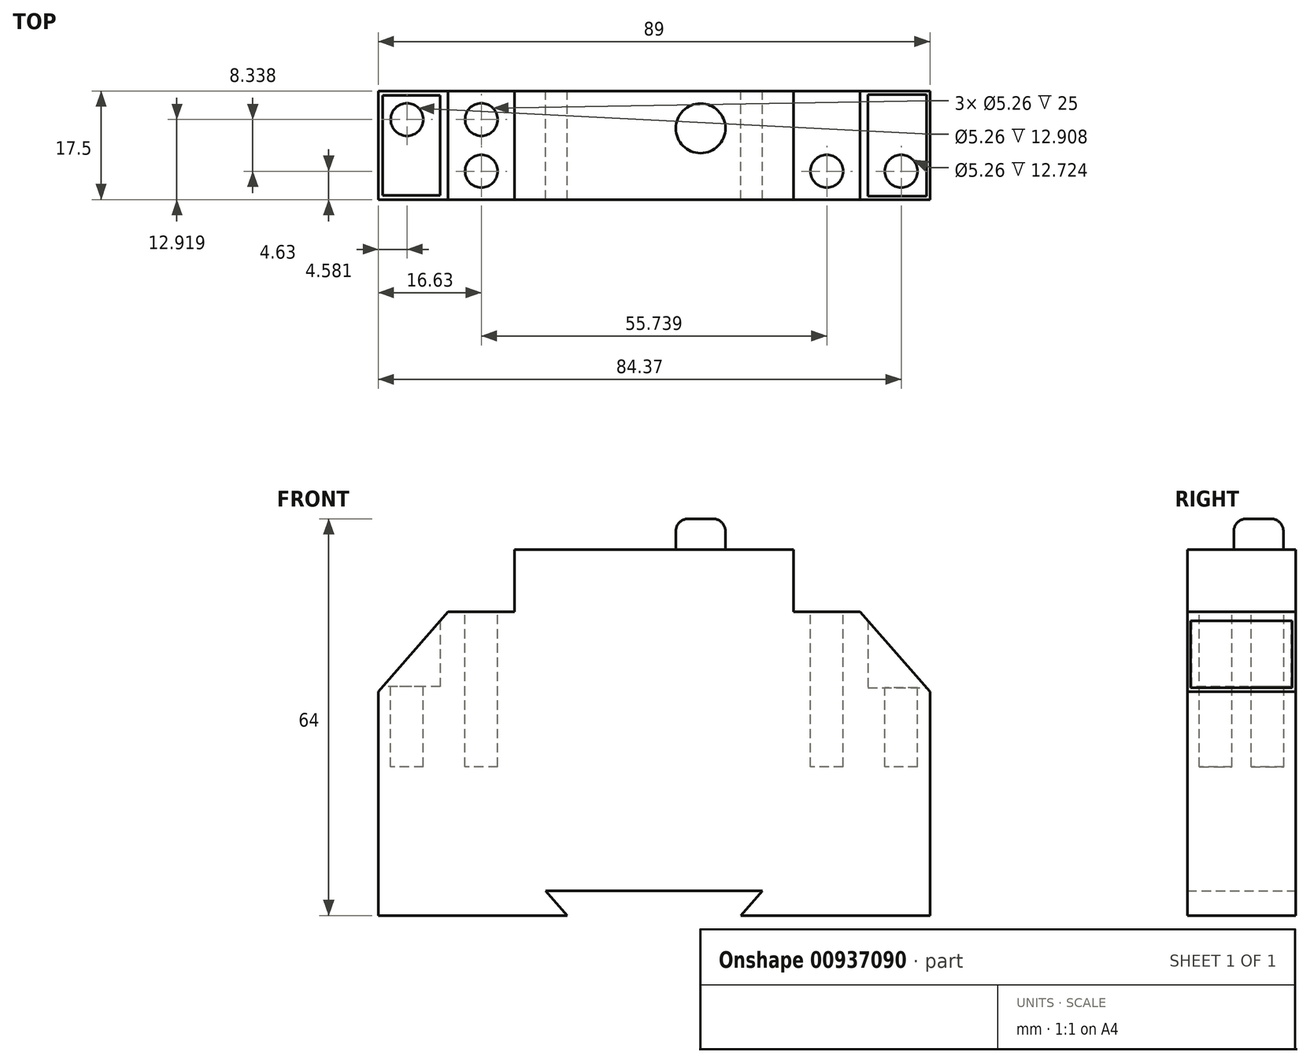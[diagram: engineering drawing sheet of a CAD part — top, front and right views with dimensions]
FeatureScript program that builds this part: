
annotation { "Feature Type Name" : "Feature", "Feature Type Description" : "" }
export const myFeature = defineFeature(function(context is Context, id is Id, definition is map)
    precondition{}
    {
        {
            var Q0;
            Q0=qCreatedBy(makeId("Front.planeOp"),FACE);
            var sketch = newSketch(context, id + "F0", { "sketchPlane" : qUnion([Q0])});
            skLineSegment(sketch, "E0.bottom", {"start": v(22.5, 29.5) * mm, "end": v(-22.5, 29.5) * mm});
            skLineSegment(sketch, "E0.top", {"start": v(44.5, -29.5) * mm, "end": v(14, -29.5) * mm});
            skLineSegment(sketch, "E0.left", {"start": v(44.5, 6.61) * mm, "end": v(44.5, -29.5) * mm});
            skLineSegment(sketch, "E0.right", {"start": v(-44.5, 6.61) * mm, "end": v(-44.5, -29.5) * mm});
            skPoint(sketch, "E0.middle", {"position": v(0, 0) * mm});
            skLineSegment(sketch, "E1.left", {"start": v(22.5, 19.5) * mm, "end": v(22.5, 29.5) * mm});
            skLineSegment(sketch, "E1.right", {"start": v(-22.5, 19.5) * mm, "end": v(-22.5, 29.5) * mm});
            skPoint(sketch, "E1.middle", {"position": v(0, 29.5) * mm});
            skLineSegment(sketch, "E2", {"start": v(-22.5, 19.5) * mm, "end": v(-33.24, 19.5) * mm});
            skLineSegment(sketch, "E3", {"start": v(-33.24, 19.5) * mm, "end": v(-44.5, 6.61) * mm});
            skLineSegment(sketch, "E4.MirrorCS", {"start": v(22.5, 19.5) * mm, "end": v(33.24, 19.5) * mm});
            skLineSegment(sketch, "E5.MirrorCS", {"start": v(33.24, 19.5) * mm, "end": v(44.5, 6.61) * mm});
            skPoint(sketch, "E6.orphan", {"position": v(-44.5, 29.5) * mm});
            skPoint(sketch, "E7.orphan", {"position": v(44.5, 29.5) * mm});
            skPoint(sketch, "E8.orphan", {"position": v(22.5, 39.5) * mm});
            skPoint(sketch, "E9.orphan", {"position": v(-22.5, 39.5) * mm});
            skPoint(sketch, "E10.middle", {"position": v(0, -29.5) * mm});
            skLineSegment(sketch, "E11", {"start": v(-17.5, -25.5) * mm, "end": v(-14, -29.5) * mm});
            skLineSegment(sketch, "E12.MirrorCS", {"start": v(17.5, -25.5) * mm, "end": v(14, -29.5) * mm});
            skLineSegment(sketch, "E13", {"start": v(-17.5, -25.5) * mm, "end": v(17.5, -25.5) * mm});
            skLineSegment(sketch, "E14.trimOffspring", {"start": v(-14, -29.5) * mm, "end": v(-44.5, -29.5) * mm});
            skSolve(sketch);
        }
        {
            var Q0;
            Q0=makeQuery(id+"F0.imprint","IMPRINT",FACE,{"disambiguationData":[TD([[makeQuery(id+"F0.imprint","IMPRINT",EDGE,{"derivedFrom":sQuery(id+"F0.wireOp",EDGE,"E0.bottom")}),1.0]])]});
            extrude(context, id + "F1", {"entities" : qUnion([Q0]), "endBound" : BoundingType.SYMMETRIC, "depth" : 17.5 * mm, "offsetDistance" : 25 * mm});
        }
        {
            var Q0;
            Q0=makeQuery(id+"F1.opExtrude","SWEPT_FACE",FACE,{"disambiguationData":[OSD([sQuery(id+"F0.wireOp",EDGE,"E0.left")])]});
            var sketch = newSketch(context, id + "F2", { "sketchPlane" : qUnion([Q0])});
            skLineSegment(sketch, "E15.bottom", {"start": v(8.75, 6.61) * mm, "end": v(-8.75, 6.61) * mm});
            skLineSegment(sketch, "E15.top", {"start": v(8.75, 19.51) * mm, "end": v(-8.75, 19.51) * mm});
            skLineSegment(sketch, "E15.left", {"start": v(8.75, 6.61) * mm, "end": v(8.75, 19.51) * mm});
            skLineSegment(sketch, "E15.right", {"start": v(-8.75, 6.61) * mm, "end": v(-8.75, 19.51) * mm});
            skPoint(sketch, "E16.middle", {"position": v(0, 16.61) * mm});
            skLineSegment(sketch, "E17", {"start": v(-8.75, 13.06) * mm, "end": v(8.75, 13.06) * mm});
            skLineSegment(sketch, "E18.bottom", {"start": v(8.2, 18.9) * mm, "end": v(-8.2, 18.9) * mm});
            skLineSegment(sketch, "E18.top", {"start": v(8.2, 7.22) * mm, "end": v(-8.2, 7.22) * mm});
            skLineSegment(sketch, "E18.left", {"start": v(8.2, 18.9) * mm, "end": v(8.2, 7.22) * mm});
            skLineSegment(sketch, "E18.right", {"start": v(-8.2, 18.9) * mm, "end": v(-8.2, 7.22) * mm});
            skPoint(sketch, "E18.middle", {"position": v(0, 13.06) * mm});
            skSolve(sketch);
        }
        {
            var Q0;
            {var subQ5=sQuery(id+"F2.wireOp",EDGE,"E16.bottom");Q0=makeQuery(id+"F2.imprint","IMPRINT",FACE,{"disambiguationData":[TD([[makeQuery(id+"F2.imprint","IMPRINT",EDGE,{"derivedFrom":subQ5}),1.0]])]});}
            var Q1;
            {var subQ5=sQuery(id+"F2.wireOp",EDGE,"E16.top");Q1=makeQuery(id+"F2.imprint","IMPRINT",FACE,{"disambiguationData":[TD([[makeQuery(id+"F2.imprint","IMPRINT",EDGE,{"derivedFrom":subQ5}),-1.0]])]});}
            var Q2;
            {var subQ5=sQuery(id+"F2.wireOp",EDGE,"E18.bottom");Q2=makeQuery(id+"F2.imprint","IMPRINT",FACE,{"disambiguationData":[TD([[makeQuery(id+"F2.imprint","IMPRINT",EDGE,{"derivedFrom":subQ5}),1.0]])]});}
            var Q3;
            {var subQ5=sQuery(id+"F2.wireOp",EDGE,"E18.top");Q3=makeQuery(id+"F2.imprint","IMPRINT",FACE,{"disambiguationData":[TD([[makeQuery(id+"F2.imprint","IMPRINT",EDGE,{"derivedFrom":subQ5}),-1.0]])]});}
            extrude(context, id + "F3", {"entities" : qUnion([Q0, Q1, Q2, Q3]), "operationType" : NewBodyOperationType.REMOVE, "oppositeDirection" : true, "depth" : 10 * mm, "offsetDistance" : 25 * mm});
        }
        {
            var Q0;
            Q0=makeQuery(id+"F1.opExtrude","SWEPT_FACE",FACE,{"disambiguationData":[OSD([sQuery(id+"F0.wireOp",EDGE,"E0.right")])]});
            var sketch = newSketch(context, id + "F4", { "sketchPlane" : qUnion([Q0])});
            skLineSegment(sketch, "E19.bottom", {"start": v(8.75, 6.61) * mm, "end": v(-8.75, 6.61) * mm});
            skLineSegment(sketch, "E19.top", {"start": v(8.75, 19.51) * mm, "end": v(-8.75, 19.51) * mm});
            skLineSegment(sketch, "E19.left", {"start": v(8.75, 6.61) * mm, "end": v(8.75, 19.51) * mm});
            skLineSegment(sketch, "E19.right", {"start": v(-8.75, 6.61) * mm, "end": v(-8.75, 19.51) * mm});
            skPoint(sketch, "E20.middle", {"position": v(0, 13.06) * mm});
            skLineSegment(sketch, "E21", {"start": v(-8.75, 13.06) * mm, "end": v(8.75, 13.06) * mm});
            skLineSegment(sketch, "E22.bottom", {"start": v(8.04, 18.72) * mm, "end": v(-8.04, 18.72) * mm});
            skLineSegment(sketch, "E22.top", {"start": v(8.04, 7.4) * mm, "end": v(-8.04, 7.4) * mm});
            skLineSegment(sketch, "E22.left", {"start": v(8.04, 18.72) * mm, "end": v(8.04, 7.4) * mm});
            skLineSegment(sketch, "E22.right", {"start": v(-8.04, 18.72) * mm, "end": v(-8.04, 7.4) * mm});
            skSolve(sketch);
        }
        {
            var Q0;
            {var subQ5=sQuery(id+"F4.wireOp",EDGE,"E20.bottom");Q0=makeQuery(id+"F4.imprint","IMPRINT",FACE,{"disambiguationData":[TD([[makeQuery(id+"F4.imprint","IMPRINT",EDGE,{"derivedFrom":subQ5}),1.0]])]});}
            var Q1;
            {var subQ5=sQuery(id+"F4.wireOp",EDGE,"E20.top");Q1=makeQuery(id+"F4.imprint","IMPRINT",FACE,{"disambiguationData":[TD([[makeQuery(id+"F4.imprint","IMPRINT",EDGE,{"derivedFrom":subQ5}),-1.0]])]});}
            var Q2;
            {var subQ5=sQuery(id+"F4.wireOp",EDGE,"E22.bottom");Q2=makeQuery(id+"F4.imprint","IMPRINT",FACE,{"disambiguationData":[TD([[makeQuery(id+"F4.imprint","IMPRINT",EDGE,{"derivedFrom":subQ5}),1.0]])]});}
            var Q3;
            {var subQ5=sQuery(id+"F4.wireOp",EDGE,"E22.top");Q3=makeQuery(id+"F4.imprint","IMPRINT",FACE,{"disambiguationData":[TD([[makeQuery(id+"F4.imprint","IMPRINT",EDGE,{"derivedFrom":subQ5}),-1.0]])]});}
            extrude(context, id + "F5", {"entities" : qUnion([Q0, Q1, Q2, Q3]), "operationType" : NewBodyOperationType.REMOVE, "oppositeDirection" : true, "depth" : 10 * mm, "offsetDistance" : 25 * mm});
        }
        {
            var Q0;
            Q0=makeQuery(id+"F1.opExtrude","SWEPT_FACE",FACE,{"disambiguationData":[OSD([sQuery(id+"F0.wireOp",EDGE,"E2")])]});
            var sketch = newSketch(context, id + "F6", { "sketchPlane" : qUnion([Q0])});
            skLineSegment(sketch, "E23", {"start": v(-27.87, 8.75) * mm, "end": v(-27.87, -8.75) * mm});
            skCircle(sketch, "E24", {"center": v(-27.87, 4.17) * mm, "radius": 2.63 * mm});
            skCircle(sketch, "E25.MirrorC", {"center": v(-27.87, -4.17) * mm, "radius": 2.63 * mm});
            skCircle(sketch, "E26.1.0.0", {"center": v(-39.87, 4.17) * mm, "radius": 2.63 * mm});
            skCircle(sketch, "E26.1.0.1", {"center": v(-39.87, -4.17) * mm, "radius": 2.63 * mm});
            skLineSegment(sketch, "E26.direction1", {"start": v(-27.87, -4.17) * mm, "end": v(-39.87, -4.17) * mm, "construction": true});
            skCircle(sketch, "E27.MirrorC", {"center": v(27.87, 4.17) * mm, "radius": 2.63 * mm});
            skCircle(sketch, "E28.MirrorC", {"center": v(27.87, -4.17) * mm, "radius": 2.63 * mm});
            skCircle(sketch, "E29.MirrorC", {"center": v(39.87, 4.17) * mm, "radius": 2.63 * mm});
            skCircle(sketch, "E30.MirrorC", {"center": v(39.87, -4.17) * mm, "radius": 2.63 * mm});
            skSolve(sketch);
        }
        {
            var Q0;
            {var subQ0=sQuery(id+"F6.wireOp",EDGE,"E25.MirrorC");var subQ1=sQuery(id+"F6.wireOp",EDGE,"E23");var subQ2=makeQuery(id+"F6.imprint","INTERSECT",VERTEX,{"disambiguationData":[OD(0.0)],"derivedFrom":[subQ1,subQ0]});Q0=makeQuery(id+"F6.imprint","IMPRINT",FACE,{"disambiguationData":[TD([[makeQuery(id+"F6.imprint","IMPRINT",EDGE,{"disambiguationData":[TD([[subQ2,-1.0]])],"derivedFrom":subQ1}),1.0]])]});}
            var Q1;
            {var subQ0=sQuery(id+"F6.wireOp",EDGE,"E25.MirrorC");var subQ1=sQuery(id+"F6.wireOp",EDGE,"E23");var subQ2=makeQuery(id+"F6.imprint","INTERSECT",VERTEX,{"disambiguationData":[OD(0.0)],"derivedFrom":[subQ1,subQ0]});Q1=makeQuery(id+"F6.imprint","IMPRINT",FACE,{"disambiguationData":[TD([[makeQuery(id+"F6.imprint","IMPRINT",EDGE,{"disambiguationData":[TD([[subQ2,-1.0]])],"derivedFrom":subQ1}),-1.0]])]});}
            var Q2;
            {var subQ0=sQuery(id+"F6.wireOp",EDGE,"E24");var subQ1=sQuery(id+"F6.wireOp",EDGE,"E23");var subQ2=makeQuery(id+"F6.imprint","INTERSECT",VERTEX,{"disambiguationData":[OD(0.0)],"derivedFrom":[subQ1,subQ0]});Q2=makeQuery(id+"F6.imprint","IMPRINT",FACE,{"disambiguationData":[TD([[makeQuery(id+"F6.imprint","IMPRINT",EDGE,{"disambiguationData":[TD([[subQ2,-1.0]])],"derivedFrom":subQ1}),-1.0]])]});}
            var Q3;
            {var subQ0=sQuery(id+"F6.wireOp",EDGE,"E24");var subQ1=sQuery(id+"F6.wireOp",EDGE,"E23");var subQ2=makeQuery(id+"F6.imprint","INTERSECT",VERTEX,{"disambiguationData":[OD(0.0)],"derivedFrom":[subQ1,subQ0]});Q3=makeQuery(id+"F6.imprint","IMPRINT",FACE,{"disambiguationData":[TD([[makeQuery(id+"F6.imprint","IMPRINT",EDGE,{"disambiguationData":[TD([[subQ2,-1.0]])],"derivedFrom":subQ1}),1.0]])]});}
            var Q4;
            Q4=makeQuery(id+"F6.imprint","IMPRINT",FACE,{"disambiguationData":[TD([[makeQuery(id+"F6.imprint","IMPRINT",EDGE,{"derivedFrom":sQuery(id+"F6.wireOp",EDGE,"E26.1.0.0")}),1.0]])]});
            var Q5;
            Q5=makeQuery(id+"F6.imprint","IMPRINT",FACE,{"disambiguationData":[TD([[makeQuery(id+"F6.imprint","IMPRINT",EDGE,{"derivedFrom":sQuery(id+"F6.wireOp",EDGE,"E26.1.0.1")}),-1.0]])]});
            var Q6;
            Q6=makeQuery(id+"F6.imprint","IMPRINT",FACE,{"disambiguationData":[TD([[makeQuery(id+"F6.imprint","IMPRINT",EDGE,{"derivedFrom":sQuery(id+"F6.wireOp",EDGE,"E27.MirrorC")}),-1.0]])]});
            var Q7;
            Q7=makeQuery(id+"F6.imprint","IMPRINT",FACE,{"disambiguationData":[TD([[makeQuery(id+"F6.imprint","IMPRINT",EDGE,{"derivedFrom":sQuery(id+"F6.wireOp",EDGE,"E28.MirrorC")}),1.0]])]});
            var Q8;
            Q8=makeQuery(id+"F6.imprint","IMPRINT",FACE,{"disambiguationData":[TD([[makeQuery(id+"F6.imprint","IMPRINT",EDGE,{"derivedFrom":sQuery(id+"F6.wireOp",EDGE,"E29.MirrorC")}),-1.0]])]});
            var Q9;
            Q9=makeQuery(id+"F6.imprint","IMPRINT",FACE,{"disambiguationData":[TD([[makeQuery(id+"F6.imprint","IMPRINT",EDGE,{"derivedFrom":sQuery(id+"F6.wireOp",EDGE,"E30.MirrorC")}),1.0]])]});
            extrude(context, id + "F7", {"entities" : qUnion([Q0, Q1, Q2, Q3, Q4, Q5, Q6, Q7, Q8, Q9]), "operationType" : NewBodyOperationType.REMOVE, "oppositeDirection" : true, "depth" : 25 * mm, "offsetDistance" : 25 * mm});
        }
        {
            var Q0;
            Q0=makeQuery(id+"F1.opExtrude","SWEPT_FACE",FACE,{"disambiguationData":[OSD([sQuery(id+"F0.wireOp",EDGE,"E0.bottom")])]});
            var sketch = newSketch(context, id + "F8", { "sketchPlane" : qUnion([Q0])});
            skCircle(sketch, "E31", {"center": v(7.5, 2.75) * mm, "radius": 4 * mm});
            skSolve(sketch);
        }
        {
            var Q0;
            Q0=makeQuery(id+"F8.imprint","IMPRINT",FACE,{"disambiguationData":[TD([[makeQuery(id+"F8.imprint","IMPRINT",EDGE,{"derivedFrom":sQuery(id+"F8.wireOp",EDGE,"E31")}),1.0]])]});
            extrude(context, id + "F9", {"entities" : qUnion([Q0]), "operationType" : NewBodyOperationType.ADD, "depth" : 5 * mm, "offsetDistance" : 25 * mm});
        }
        {
            var Q0;
            Q0=makeQuery(id+"F9.opExtrude","CAP_EDGE",EDGE,{"disambiguationData":[OSD([sQuery(id+"F8.wireOp",EDGE,"E31")])],"isStart":false});
            fillet(context, id + "F10", {"entities" : qUnion([Q0]), "radius" : 2 * mm, "tangentPropagation" : true, "allowEdgeOverflow" : false});
        }
    });
